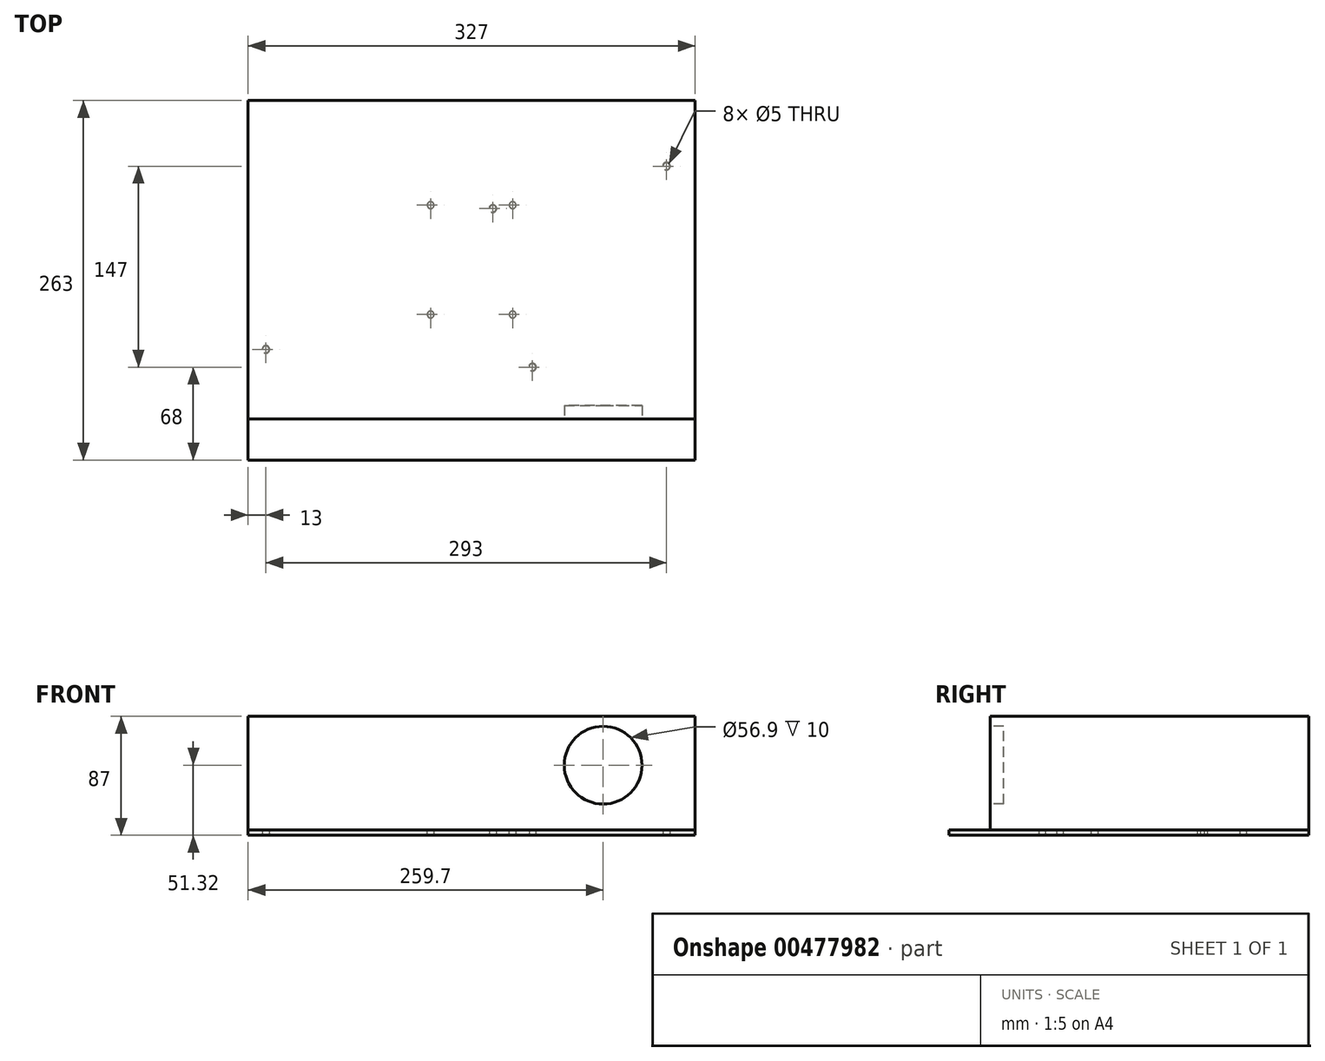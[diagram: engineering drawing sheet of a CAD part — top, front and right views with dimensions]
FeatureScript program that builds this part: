
annotation { "Feature Type Name" : "Feature", "Feature Type Description" : "" }
export const myFeature = defineFeature(function(context is Context, id is Id, definition is map)
    precondition{}
    {
        {
            var Q0;
            Q0=qCreatedBy(makeId("Front.planeOp"),FACE);
            var sketch = newSketch(context, id + "F0", { "sketchPlane" : qUnion([Q0])});
            skLineSegment(sketch, "E0.bottom", {"start": v(-163.5, 83) * mm, "end": v(163.5, 83) * mm});
            skLineSegment(sketch, "E0.top", {"start": v(-163.5, 0) * mm, "end": v(163.5, 0) * mm});
            skLineSegment(sketch, "E0.left", {"start": v(-163.5, 83) * mm, "end": v(-163.5, 0) * mm});
            skLineSegment(sketch, "E1", {"start": v(163.5, 0) * mm, "end": v(163.5, 83) * mm});
            skSolve(sketch);
        }
        {
            var Q0;
            Q0 = qSketchRegion(id + "F0", true);
            extrude(context, id + "F1", {"entities" : qUnion([Q0]), "oppositeDirection" : true, "depth" : 233 * mm});
        }
        {
            var Q0;
            Q0=makeQuery(id+"F1.opExtrude","CAP_FACE",FACE,{"disambiguationData":[OSD([sQuery(id+"F0.wireOp",EDGE,"E0.bottom"),sQuery(id+"F0.wireOp",EDGE,"E0.top"),sQuery(id+"F0.wireOp",EDGE,"E0.left"),sQuery(id+"F0.wireOp",EDGE,"E1")])],"isStart":true});
            var sketch = newSketch(context, id + "F2", { "sketchPlane" : qUnion([Q0])});
            skPoint(sketch, "E2", {"position": v(96.2, 47.32) * mm});
            skCircle(sketch, "E3", {"center": v(96.2, 47.32) * mm, "radius": 28.45 * mm});
            skSolve(sketch);
        }
        {
            var Q0;
            Q0 = qSketchRegion(id + "F2", true);
            extrude(context, id + "F3", {"entities" : qUnion([Q0]), "operationType" : NewBodyOperationType.REMOVE, "oppositeDirection" : true, "depth" : 10 * mm});
        }
        {
            var Q0;
            Q0=makeQuery(id+"F1.opExtrude","SWEPT_FACE",FACE,{"disambiguationData":[OSD([sQuery(id+"F0.wireOp",EDGE,"E0.top")])]});
            var sketch = newSketch(context, id + "F4", { "sketchPlane" : qUnion([Q0])});
            skLineSegment(sketch, "E4.bottom", {"start": v(-163.5, -233) * mm, "end": v(163.5, -233) * mm});
            skLineSegment(sketch, "E4.top", {"start": v(-163.5, 30) * mm, "end": v(163.5, 30) * mm});
            skLineSegment(sketch, "E4.left", {"start": v(-163.5, -233) * mm, "end": v(-163.5, 30) * mm});
            skLineSegment(sketch, "E4.right", {"start": v(163.5, -233) * mm, "end": v(163.5, 30) * mm});
            skLineSegment(sketch, "E5.bottom", {"start": v(-30, -76.5) * mm, "end": v(30, -76.5) * mm, "construction": true});
            skLineSegment(sketch, "E5.top", {"start": v(-30, -156.5) * mm, "end": v(30, -156.5) * mm, "construction": true});
            skLineSegment(sketch, "E5.left", {"start": v(-30, -76.5) * mm, "end": v(-30, -156.5) * mm, "construction": true});
            skLineSegment(sketch, "E5.right", {"start": v(30, -76.5) * mm, "end": v(30, -156.5) * mm, "construction": true});
            skPoint(sketch, "E5.middle", {"position": v(0, -116.5) * mm});
            skLineSegment(sketch, "E6", {"start": v(0, 0) * mm, "end": v(0, -233) * mm, "construction": true});
            skPoint(sketch, "E7", {"position": v(-30, -156.5) * mm});
            skPoint(sketch, "E8", {"position": v(30, -156.5) * mm});
            skPoint(sketch, "E9", {"position": v(30, -76.5) * mm});
            skPoint(sketch, "E10", {"position": v(-30, -76.5) * mm});
            skSolve(sketch);
        }
        {
            var Q0;
            Q0 = qSketchRegion(id + "F4", true);
            extrude(context, id + "F5", {"entities" : qUnion([Q0]), "depth" : 4 * mm});
        }
        {
            var Q0;
            Q0=makeQuery(id+"F5.opExtrude","CAP_FACE",FACE,{"disambiguationData":[OSD([sQuery(id+"F4.wireOp",EDGE,"E4.bottom"),sQuery(id+"F4.wireOp",EDGE,"E4.top"),sQuery(id+"F4.wireOp",EDGE,"E4.left"),sQuery(id+"F4.wireOp",EDGE,"E4.right")])],"isStart":false});
            var sketch = newSketch(context, id + "F6", { "sketchPlane" : qUnion([Q0])});
            skPoint(sketch, "E11", {"position": v(142.5, -185) * mm});
            skPoint(sketch, "E12", {"position": v(15.5, -154) * mm});
            skPoint(sketch, "E13", {"position": v(44.5, -38) * mm});
            skPoint(sketch, "E14", {"position": v(-150.5, -51) * mm});
            skSolve(sketch);
        }
        {
            var Q0;
            Q0=sQuery(id+"F6.wireOp",VERTEX,"E11");
            var Q1;
            Q1=sQuery(id+"F6.wireOp",VERTEX,"E13");
            var Q2;
            Q2=sQuery(id+"F6.wireOp",VERTEX,"E14");
            var Q3;
            Q3=sQuery(id+"F6.wireOp",VERTEX,"E12");
            var Q4;
            Q4=makeQuery(id+"F5.opExtrude","SWEPT_BODY",BODY,{"disambiguationData":[OSD([sQuery(id+"F4.wireOp",EDGE,"E4.bottom"),sQuery(id+"F4.wireOp",EDGE,"E4.top"),sQuery(id+"F4.wireOp",EDGE,"E4.left"),sQuery(id+"F4.wireOp",EDGE,"E4.right")])]});
            hole(context, id + "F7", {"style" : HoleStyle.C_SINK, "endStyle" : HoleEndStyle.THROUGH, "holeDiameter" : 5 * mm, "cSinkDiameter" : 5.5 * mm, "cSinkAngle" : 90 * degree, "isTappedThrough" : true, "tappedDepth" : 12 * mm, "tapClearance" : 3, "locations" : qUnion([Q0, Q1, Q2, Q3]), "scope" : qUnion([Q4])});
        }
        {
            var Q0;
            Q0=sQuery(id+"F4.wireOp",VERTEX,"E7");
            var Q1;
            Q1=sQuery(id+"F4.wireOp",VERTEX,"E8");
            var Q2;
            Q2=sQuery(id+"F4.wireOp",VERTEX,"E9");
            var Q3;
            Q3=sQuery(id+"F4.wireOp",VERTEX,"E10");
            var Q4;
            Q4=makeQuery(id+"F5.opExtrude","SWEPT_BODY",BODY,{"disambiguationData":[OSD([sQuery(id+"F4.wireOp",EDGE,"E4.bottom"),sQuery(id+"F4.wireOp",EDGE,"E4.top"),sQuery(id+"F4.wireOp",EDGE,"E4.left"),sQuery(id+"F4.wireOp",EDGE,"E4.right")])]});
            hole(context, id + "F8", {"style" : HoleStyle.SIMPLE, "endStyle" : HoleEndStyle.THROUGH, "oppositeDirection" : true, "holeDiameter" : 5 * mm, "isTappedThrough" : true, "tappedDepth" : 12 * mm, "tapClearance" : 3, "locations" : qUnion([Q0, Q1, Q2, Q3]), "scope" : qUnion([Q4])});
        }
    });
